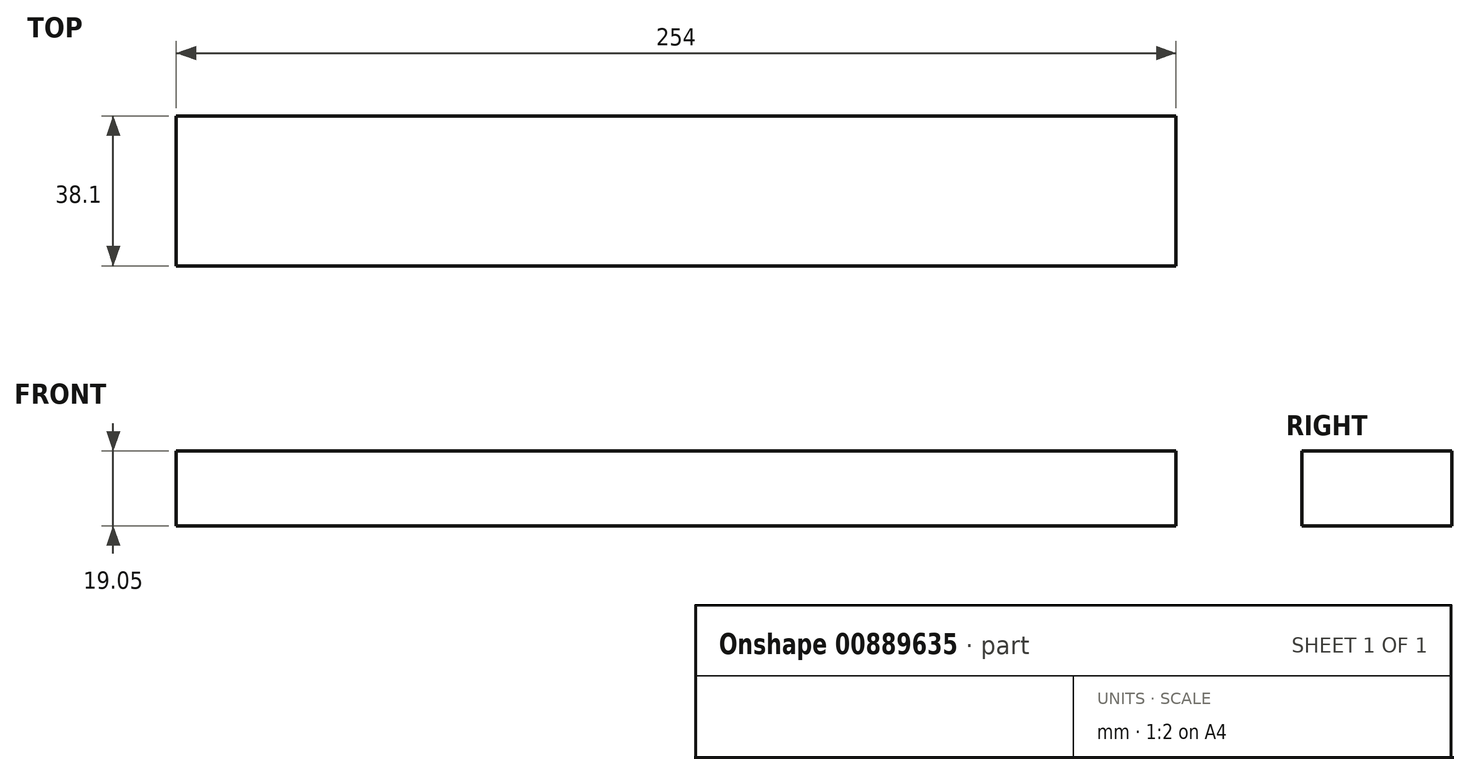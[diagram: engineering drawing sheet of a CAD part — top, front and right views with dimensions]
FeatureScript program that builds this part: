
annotation { "Feature Type Name" : "Feature", "Feature Type Description" : "" }
export const myFeature = defineFeature(function(context is Context, id is Id, definition is map)
    precondition{}
    {
        {
            var Q0;
            Q0=qCreatedBy(makeId("Front.planeOp"),FACE);
            var sketch = newSketch(context, id + "F0", { "sketchPlane" : qUnion([Q0])});
            skLineSegment(sketch, "E0.bottom", {"start": v(0, 0) * mm, "end": v(254, 0) * mm});
            skLineSegment(sketch, "E0.top", {"start": v(0, 19.05) * mm, "end": v(254, 19.05) * mm});
            skLineSegment(sketch, "E0.left", {"start": v(0, 0) * mm, "end": v(0, 19.05) * mm});
            skLineSegment(sketch, "E0.right", {"start": v(254, 0) * mm, "end": v(254, 19.05) * mm});
            skSolve(sketch);
        }
        {
            var Q0;
            Q0 = qSketchRegion(id + "F0", true);
            extrude(context, id + "F1", {"entities" : qUnion([Q0]), "depth" : 38.1 * mm, "offsetDistance" : 25.4 * mm});
        }
    });
